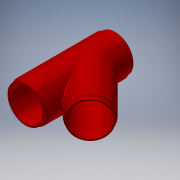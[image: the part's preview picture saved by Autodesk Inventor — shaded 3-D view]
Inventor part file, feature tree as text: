
AUTODESK INVENTOR PART (.ipt)
format: ipt  version: 2017.3 (Build 213257000, 257)  size: 296,960 bytes
history: native  units: in
note: dims shown in document units (in); Inventor stores cm internally (conversion verified against a paired STEP export)
features: extrude x18, sketch x14, fillet x6, chamfer x3, plane x1, projected_geometry x1
ambient origin geometry x8: Origin, YZ Plane, XZ Plane, XY Plane, X Axis, Y Axis, Z Axis, Center Point
bodies: Solid1 (feature_tree)
feature tree (43):
  sketch  "Sketch1"  dims[d0=26.5in d1=29.0in]
  extrude  "Extrusion1"  Depth=29.0in
  plane  "Work Plane1"
  sketch  "Sketch2"  dims[d2=31.0in d3=50.9921in d4=19.4961in d5=0.0in d6=0.0in]
  extrude  "Extrusion2"  Depth=50.9921in TaperAngle=0.0deg
  extrude  "Extrusion3"  Depth=26.5in
  extrude  "Extrusion4"  Depth=31.0in
  extrude  "Extrusion5"  Depth=28.0in
  extrude  "Extrusion6"  Depth=28.0in
  extrude  "Extrusion7"  TaperAngle=0.0deg  [1 undecoded]
  extrude  "Extrusion8"  Depth=0.5in
  extrude  "Extrusion9"  Depth=47.9921in
  fillet  "Fillet1"  Radius=16.4961in
  fillet  "Fillet2"  [1 undecoded]
  fillet  "Fillet3"  Radius=47.9921in
  fillet  "Fillet4"  [1 undecoded]
  extrude  "Extrusion10"  TaperAngle=0.0deg  [1 undecoded]
  extrude  "Extrusion11"  TaperAngle=0.0deg  [1 undecoded]
  extrude  "Extrusion12"  Depth=6.0in
  fillet  "Fillet5"  Radius=1.0in
  chamfer  "Chamfer3"  Distance=1.0in
  fillet  "Fillet6"  Radius=30.48in
  chamfer  "Chamfer4"  Distance=1.0in
  extrude  "Extrusion15"  Depth=30.48in
  extrude  "Extrusion17"  Depth=1.0in TaperAngle=0.0deg
  extrude  "Extrusion19"  Depth=0.0312in
  chamfer  "Chamfer6"  Distance=0.74in
  extrude  "Extrusion21"  Depth=0.125in TaperAngle=45.0deg
  extrude  "Extrusion22"  Depth=0.0312in
  extrude  "Extrusion23"  Depth=0.0312in TaperAngle=45.0deg
  sketch  "Sketch3"  dims[d7=45.0deg d8=26.5in]
  sketch  "Sketch4"  dims[d9=29.0in d10=31.0in]
  sketch  "Sketch5"  dims[d11=50.9921in d12=0.0in d13=28.0in]
  sketch  "Sketch6"  dims[d14=0.5in d15=0.0in d16=28.0in]
  sketch  "Sketch7"  dims[d17=0.5in d18=0.0in]
  sketch  "Sketch8"  dims[d19=28.0in d20=0.5in]
  sketch  "Sketch11"  dims[d21=0.0in d22=47.9921in d23=16.4961in d24=0.0in d25=0.0in d26=47.9921in d27=0.0in]
  sketch  "Sketch13"  dims[d28=50.9921in d29=0.0in]
  projected_geometry  "Projected Loop4"
  sketch  "Sketch15"  dims[d30=50.9921in d31=0.0in]
  sketch  "Sketch17"  dims[d32=1.0in d33=6.0in d34=1.0in]
  sketch  "Sketch18"  dims[d35=1.0in]
  sketch  "Sketch19"  dims[d39=30.48in d40=1.0in d41=0.0in d42=30.48in d43=1.0in d44=0.0in d45=30.48in d46=1.0in d47=0.0in d48=0.0312in d52=0.74in d53=0.125in d54=45.0deg d55=0.0312in d56=0.0312in d57=0.125in d58=45.0deg d66=1.0in d67=0.0in d76=1.0in d77=0.0in d83=1.0in d84=0.0in d85=0.26in d86=0.125in d87=45.0deg d93=1.0in d94=0.0in d95=1.0in d96=0.0in d97=1.0in d98=0.0in]
note: 5 required parameter values undecoded (feature->parameter linkage not recoverable at this tier; creation-order binding heuristic only, values carry confidence <= 0.55)
